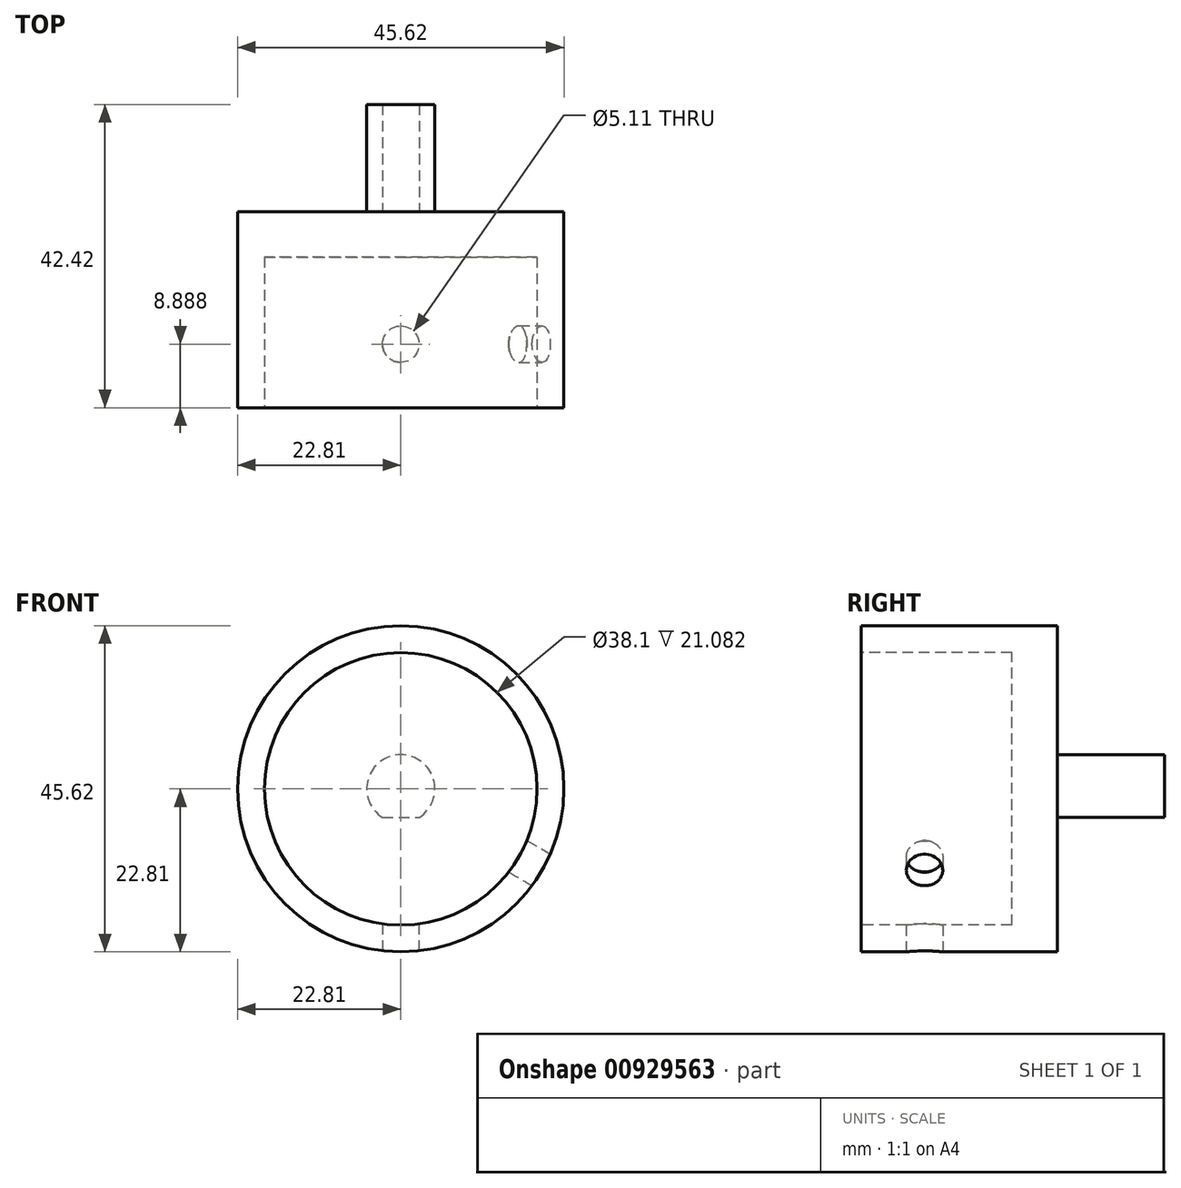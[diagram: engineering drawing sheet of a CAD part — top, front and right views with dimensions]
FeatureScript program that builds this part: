
annotation { "Feature Type Name" : "Feature", "Feature Type Description" : "" }
export const myFeature = defineFeature(function(context is Context, id is Id, definition is map)
    precondition{}
    {
        {
            var Q0;
            Q0=qCreatedBy(makeId("Front.planeOp"),FACE);
            var sketch = newSketch(context, id + "F0", { "sketchPlane" : qUnion([Q0])});
            skCircle(sketch, "E0", {"center": v(0, 0) * mm, "radius": 22.8 * mm});
            skSolve(sketch);
        }
        {
            var Q0;
            Q0=makeQuery(id+"F0.imprint","IMPRINT",FACE,{"disambiguationData":[TD([[makeQuery(id+"F0.imprint","IMPRINT",EDGE,{"derivedFrom":sQuery(id+"F0.wireOp",EDGE,"E0")}),1.0]])]});
            extrude(context, id + "F1", {"entities" : qUnion([Q0]), "depth" : 27.43 * mm, "offsetDistance" : 25.4 * mm});
        }
        {
            var Q0;
            Q0=makeQuery(id+"F1.opExtrude","CAP_FACE",FACE,{"disambiguationData":[OSD([sQuery(id+"F0.wireOp",EDGE,"E0")])],"isStart":true});
            var sketch = newSketch(context, id + "F2", { "sketchPlane" : qUnion([Q0])});
            skArc(sketch, "E1", {"start": v(2.58, -4) * mm, "mid": v(0, 4.76) * mm, "end": v(-2.58, -4) * mm});
            skLineSegment(sketch, "E2", {"start": v(0, 0) * mm, "end": v(0, -4) * mm});
            skLineSegment(sketch, "E3", {"start": v(2.58, -4) * mm, "end": v(-2.58, -4) * mm});
            skPoint(sketch, "E4.orphan", {"position": v(3.82, -4) * mm});
            skSolve(sketch);
        }
        {
            var Q0;
            Q0=makeQuery(id+"F2.imprint","IMPRINT",FACE,{"disambiguationData":[TD([[makeQuery(id+"F2.imprint","IMPRINT",EDGE,{"derivedFrom":sQuery(id+"F2.wireOp",EDGE,"E1")}),1.0]])]});
            extrude(context, id + "F3", {"entities" : qUnion([Q0]), "operationType" : NewBodyOperationType.ADD, "depth" : 15 * mm, "offsetDistance" : 25.4 * mm});
        }
        {
            var Q0;
            Q0=makeQuery(id+"F1.opExtrude","CAP_FACE",FACE,{"disambiguationData":[OSD([sQuery(id+"F0.wireOp",EDGE,"E0")])],"isStart":false});
            var sketch = newSketch(context, id + "F4", { "sketchPlane" : qUnion([Q0])});
            skCircle(sketch, "E5", {"center": v(0, 0) * mm, "radius": 19.05 * mm});
            skSolve(sketch);
        }
        {
            var Q0;
            Q0=makeQuery(id+"F4.imprint","IMPRINT",FACE,{"disambiguationData":[TD([[makeQuery(id+"F4.imprint","IMPRINT",EDGE,{"derivedFrom":sQuery(id+"F4.wireOp",EDGE,"E5")}),1.0]])]});
            extrude(context, id + "F5", {"entities" : qUnion([Q0]), "operationType" : NewBodyOperationType.REMOVE, "oppositeDirection" : true, "depth" : 21.08 * mm, "offsetDistance" : 25.4 * mm});
        }
        {
            var Q0;
            Q0=qCreatedBy(makeId("Top.planeOp"),FACE);
            cPlane(context, id + "F6", {"entities" : qUnion([Q0]), "cplaneType" : CPlaneType.OFFSET, "offset" : 22.8 * mm, "oppositeDirection" : true, "width" : 152.4 * mm, "height" : 152.4 * mm});
        }
        {
            var Q0;
            Q0=qCreatedBy(id+"F6.planeOp",FACE);
            var sketch = newSketch(context, id + "F7", { "sketchPlane" : qUnion([Q0])});
            skPoint(sketch, "E6", {"position": v(0, -18.54) * mm});
            skSolve(sketch);
        }
        {
            var Q0;
            Q0=sQuery(id+"F7.wireOp",VERTEX,"E6");
            var Q1;
            Q1=makeQuery(id+"F1.opExtrude","SWEPT_BODY",BODY,{"disambiguationData":[OSD([sQuery(id+"F0.wireOp",EDGE,"E0")])]});
            hole(context, id + "F8", {"style" : HoleStyle.SIMPLE, "endStyle" : HoleEndStyle.BLIND, "oppositeDirection" : true, "standardTappedOrClearance" : lookupTablePath({ "standard" : "ANSI", "engagement" : "75%", "pitch" : "20 tpi", "size" : "1/4", "type" : "Tapped" }), "standardBlindInLast" : lookupTablePath({ "standard" : "ANSI", "fit" : "Normal", "engagement" : "75%", "pitch" : "20 tpi", "size" : "1/4", "type" : "Clearance & tapped" }), "holeDiameter" : 5.1 * mm, "majorDiameter" : 6.35 * mm, "showTappedDepth" : true, "holeDepth" : 7.57 * mm, "isTappedThrough" : true, "tappedDepth" : 3.76 * mm, "tapClearance" : 3, "locations" : qUnion([Q0]), "scope" : qUnion([Q1])});
        }
        {
            var Q0;
            Q0=makeQuery(id+"F1.opExtrude","CAP_EDGE",EDGE,{"disambiguationData":[OSD([sQuery(id+"F0.wireOp",EDGE,"E0")])],"isStart":false});
            var Q1;
            Q1=qCreatedBy(id+"F6.planeOp",FACE);
            cPlane(context, id + "F9", {"entities" : qUnion([Q0, Q1]), "cplaneType" : CPlaneType.LINE_ANGLE, "offset" : 25.4 * mm, "angle" : 60 * degree, "width" : 152.4 * mm, "height" : 152.4 * mm});
        }
        {
            var Q0;
            Q0=qCreatedBy(id+"F9.planeOp",FACE);
            cPlane(context, id + "F10", {"entities" : qUnion([Q0]), "cplaneType" : CPlaneType.OFFSET, "offset" : 22.8 * mm, "width" : 152.4 * mm, "height" : 152.4 * mm});
        }
        {
            var Q0;
            Q0=qCreatedBy(id+"F10.planeOp",FACE);
            var sketch = newSketch(context, id + "F11", { "sketchPlane" : qUnion([Q0])});
            skPoint(sketch, "E7", {"position": v(-18.54, 0) * mm});
            skSolve(sketch);
        }
        {
            var Q0;
            Q0=sQuery(id+"F11.wireOp",VERTEX,"E7");
            var Q1;
            Q1=makeQuery(id+"F1.opExtrude","SWEPT_BODY",BODY,{"disambiguationData":[OSD([sQuery(id+"F0.wireOp",EDGE,"E0")])]});
            hole(context, id + "F12", {"style" : HoleStyle.SIMPLE, "endStyle" : HoleEndStyle.BLIND, "standardTappedOrClearance" : lookupTablePath({ "standard" : "ANSI", "engagement" : "75%", "pitch" : "20 tpi", "size" : "1/4", "type" : "Tapped" }), "standardBlindInLast" : lookupTablePath({ "standard" : "ANSI", "fit" : "Normal", "engagement" : "75%", "pitch" : "20 tpi", "size" : "1/4", "type" : "Clearance & tapped" }), "holeDiameter" : 5.1 * mm, "majorDiameter" : 6.35 * mm, "showTappedDepth" : true, "holeDepth" : 3.76 * mm, "isTappedThrough" : true, "tappedDepth" : 3.76 * mm, "tapClearance" : 3, "locations" : qUnion([Q0]), "scope" : qUnion([Q1])});
        }
    });
